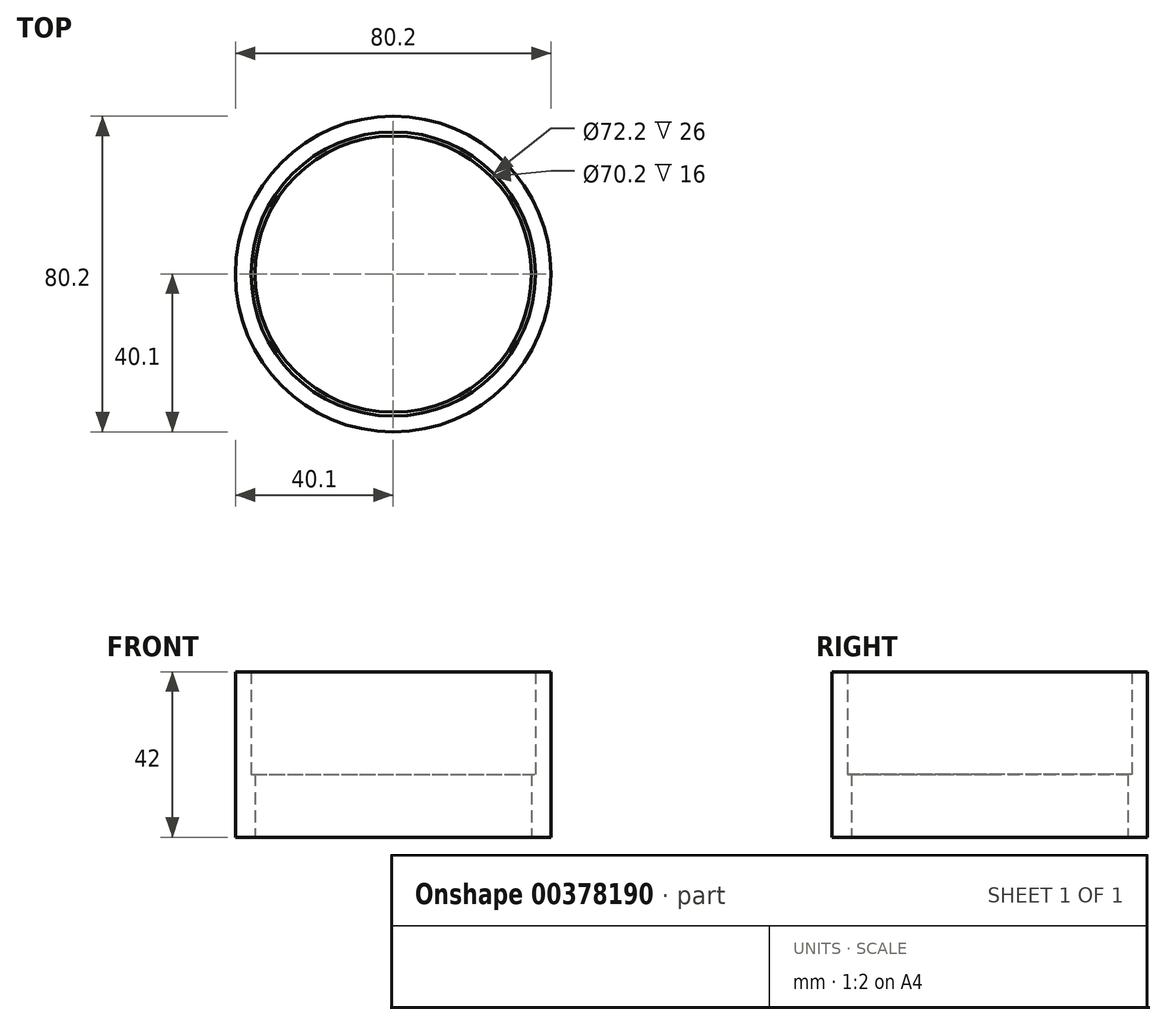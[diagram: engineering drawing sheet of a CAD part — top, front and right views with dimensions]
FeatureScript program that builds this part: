
annotation { "Feature Type Name" : "Feature", "Feature Type Description" : "" }
export const myFeature = defineFeature(function(context is Context, id is Id, definition is map)
    precondition{}
    {
        {
            var Q0;
            Q0=qCreatedBy(makeId("Front.planeOp"),FACE);
            var sketch = newSketch(context, id + "F0", { "sketchPlane" : qUnion([Q0])});
            skLineSegment(sketch, "E0", {"start": v(-36.1, -15.61) * mm, "end": v(-35.1, -15.61) * mm});
            skLineSegment(sketch, "E1", {"start": v(-35.1, -15.61) * mm, "end": v(-35.1, -31.61) * mm});
            skLineSegment(sketch, "E2", {"start": v(-35.1, -31.61) * mm, "end": v(-40.1, -31.61) * mm});
            skLineSegment(sketch, "E3", {"start": v(-40.1, -31.61) * mm, "end": v(-40.1, 10.39) * mm});
            skLineSegment(sketch, "E4", {"start": v(-40.1, 10.39) * mm, "end": v(-36.1, 10.39) * mm});
            skLineSegment(sketch, "E5", {"start": v(-36.1, -15.61) * mm, "end": v(-36.1, 10.39) * mm});
            skLineSegment(sketch, "E6", {"start": v(0, -27) * mm, "end": v(0, 35.98) * mm});
            skLineSegment(sketch, "E7.bottom", {"start": v(0, 29.13) * mm, "end": v(-24.34, 29.13) * mm});
            skLineSegment(sketch, "E7.top", {"start": v(0, 41.8) * mm, "end": v(-24.34, 41.8) * mm});
            skLineSegment(sketch, "E7.left", {"start": v(0, 29.13) * mm, "end": v(0, 41.8) * mm});
            skLineSegment(sketch, "E7.right", {"start": v(-24.34, 29.13) * mm, "end": v(-24.34, 41.8) * mm});
            skSolve(sketch);
        }
        {
            var Q0;
            Q0=makeQuery(id+"F0.imprint","IMPRINT",FACE,{"disambiguationData":[TD([[makeQuery(id+"F0.imprint","IMPRINT",EDGE,{"derivedFrom":sQuery(id+"F0.wireOp",EDGE,"E0")}),-1.0]])]});
            var Q1;
            Q1=sQuery(id+"F0.wireOp",EDGE,"E7.left");
            revolve(context, id + "F1", {"entities" : qUnion([Q0]), "axis" : qUnion([Q1]), "revolveType" : RevolveType.FULL});
        }
    });
